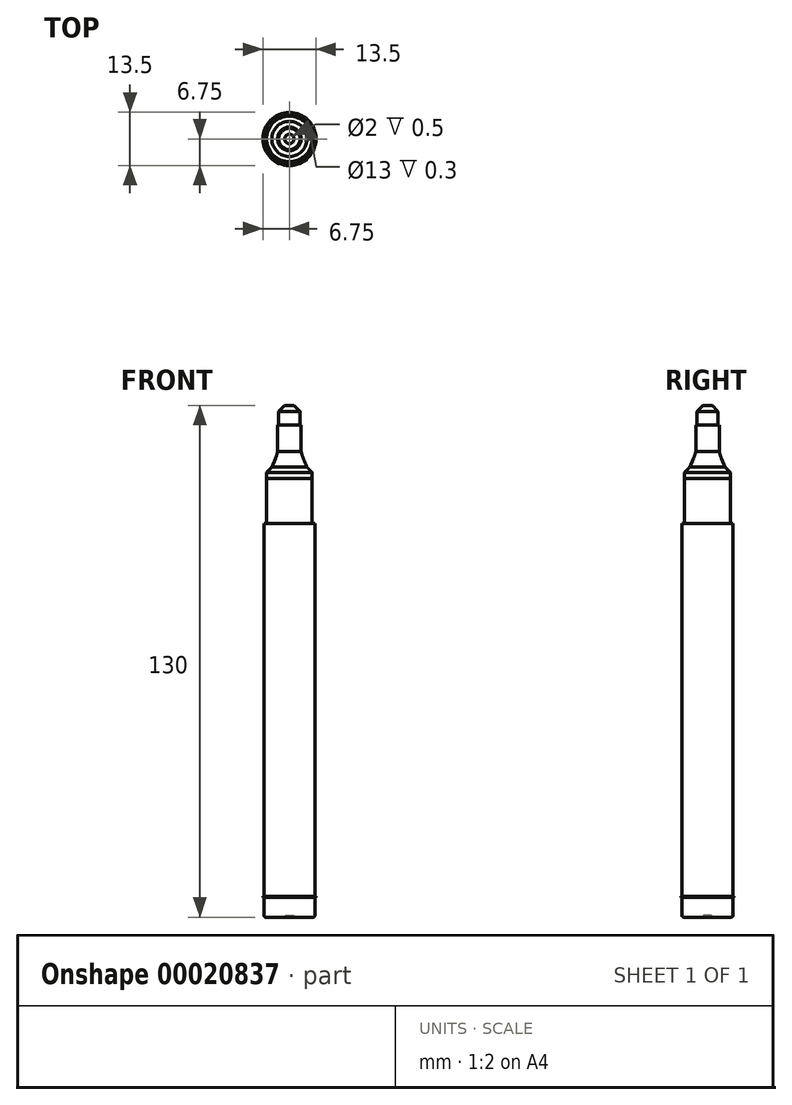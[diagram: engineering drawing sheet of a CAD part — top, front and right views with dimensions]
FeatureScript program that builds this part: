
annotation { "Feature Type Name" : "Feature", "Feature Type Description" : "" }
export const myFeature = defineFeature(function(context is Context, id is Id, definition is map)
    precondition{}
    {
        {
            var Q0;
            Q0=qCreatedBy(makeId("Top.planeOp"),FACE);
            var sketch = newSketch(context, id + "F0", { "sketchPlane" : qUnion([Q0])});
            skCircle(sketch, "E0", {"center": v(0, 0) * mm, "radius": 6.5 * mm});
            skSolve(sketch);
        }
        {
            var Q0;
            Q0 = qSketchRegion(id + "F0", true);
            extrude(context, id + "F1", {"entities" : qUnion([Q0]), "depth" : 5 * mm});
        }
        {
            var Q0;
            Q0=makeQuery(id+"F1.opExtrude","CAP_FACE",FACE,{"disambiguationData":[OSD([sQuery(id+"F0.wireOp",EDGE,"E0")])],"isStart":true});
            var sketch = newSketch(context, id + "F2", { "sketchPlane" : qUnion([Q0])});
            skCircle(sketch, "E1", {"center": v(0, 0) * mm, "radius": 1 * mm});
            skCircle(sketch, "E2", {"center": v(0, 0) * mm, "radius": 0.15 * mm});
            skSolve(sketch);
        }
        {
            var Q0;
            Q0 = qSketchRegion(id + "F2", true);
            extrude(context, id + "F3", {"entities" : qUnion([Q0]), "operationType" : NewBodyOperationType.REMOVE, "oppositeDirection" : true, "depth" : .5 * mm});
        }
        {
            var Q0;
            Q0=makeQuery(id+"F1.opExtrude","CAP_EDGE",EDGE,{"disambiguationData":[OSD([sQuery(id+"F0.wireOp",EDGE,"E0")])],"isStart":true});
            fillet(context, id + "F4", {"entities" : qUnion([Q0]), "radius" : .5 * mm, "tangentPropagation" : true, "allowEdgeOverflow" : false});
        }
        {
            var Q0;
            Q0=makeQuery(id+"F1.opExtrude","CAP_FACE",FACE,{"disambiguationData":[OSD([sQuery(id+"F0.wireOp",EDGE,"E0")])],"isStart":false});
            var sketch = newSketch(context, id + "F5", { "sketchPlane" : qUnion([Q0])});
            skCircle(sketch, "E3", {"center": v(0, 0) * mm, "radius": 6.75 * mm});
            skCircle(sketch, "E4", {"center": v(0, 0) * mm, "radius": 6.5 * mm});
            skSolve(sketch);
        }
        {
            var Q0;
            Q0 = qSketchRegion(id + "F5", true);
            extrude(context, id + "F6", {"entities" : qUnion([Q0]), "depth" : .3 * mm});
        }
        {
            var Q0;
            Q0=makeQuery(id+"F1.opExtrude","CAP_FACE",FACE,{"disambiguationData":[OSD([sQuery(id+"F0.wireOp",EDGE,"E0")])],"isStart":false});
            var sketch = newSketch(context, id + "F7", { "sketchPlane" : qUnion([Q0])});
            skCircle(sketch, "E5", {"center": v(0, 0) * mm, "radius": 6.9 * mm});
            skCircle(sketch, "E6", {"center": v(0, 0) * mm, "radius": 6.75 * mm});
            skSolve(sketch);
        }
        {
            var Q0;
            Q0=sQuery(id+"F7.wireOp",EDGE,"E5");
            var Q1;
            Q1=sQuery(id+"F7.wireOp",EDGE,"E6");
            extrude(context, id + "F8", {"bodyType" : ToolBodyType.SURFACE, "surfaceEntities" : qUnion([Q0, Q1]), "depth" : .5 * mm});
        }
        {
            var Q0;
            Q0=makeQuery(id+"F1.opExtrude","CAP_FACE",FACE,{"disambiguationData":[OSD([sQuery(id+"F0.wireOp",EDGE,"E0")])],"isStart":false});
            var sketch = newSketch(context, id + "F9", { "sketchPlane" : qUnion([Q0])});
            skCircle(sketch, "E7", {"center": v(0, 0) * mm, "radius": 6.5 * mm});
            skSolve(sketch);
        }
        {
            var Q0;
            Q0 = qSketchRegion(id + "F9", true);
            extrude(context, id + "F10", {"entities" : qUnion([Q0]), "depth" : 93 * mm});
        }
        {
            var Q0;
            Q0=makeQuery(id+"F10.opExtrude","CAP_FACE",FACE,{"disambiguationData":[OSD([sQuery(id+"F9.wireOp",EDGE,"E7")])],"isStart":false});
            var sketch = newSketch(context, id + "F11", { "sketchPlane" : qUnion([Q0])});
            skCircle(sketch, "E8", {"center": v(0, 0) * mm, "radius": 6.5 * mm});
            skSolve(sketch);
        }
        {
            var Q0;
            Q0 = qSketchRegion(id + "F11", true);
            extrude(context, id + "F12", {"entities" : qUnion([Q0]), "operationType" : NewBodyOperationType.ADD, "depth" : 2 * mm});
        }
        {
            var Q0;
            Q0=makeQuery(id+"F12.opExtrude","CAP_FACE",FACE,{"disambiguationData":[OSD([sQuery(id+"F11.wireOp",EDGE,"E8")])],"isStart":false});
            var sketch = newSketch(context, id + "F13", { "sketchPlane" : qUnion([Q0])});
            skCircle(sketch, "E9", {"center": v(0, 0) * mm, "radius": 5.8 * mm});
            skSolve(sketch);
        }
        {
            var Q0;
            Q0 = qSketchRegion(id + "F13", true);
            extrude(context, id + "F14", {"entities" : qUnion([Q0]), "depth" : 11.5 * mm});
        }
        {
            var Q0;
            Q0=makeQuery(id+"F14.opExtrude","CAP_FACE",FACE,{"disambiguationData":[OSD([sQuery(id+"F13.wireOp",EDGE,"E9")])],"isStart":false});
            var sketch = newSketch(context, id + "F15", { "sketchPlane" : qUnion([Q0])});
            skCircle(sketch, "E10", {"center": v(0, 0) * mm, "radius": 5.8 * mm});
            skSolve(sketch);
        }
        {
            var Q0;
            Q0 = qSketchRegion(id + "F15", true);
            extrude(context, id + "F16", {"entities" : qUnion([Q0]), "depth" : 6.5 * mm});
        }
        {
            var Q0;
            Q0=makeQuery(id+"F16.opExtrude","CAP_FACE",FACE,{"disambiguationData":[OSD([sQuery(id+"F15.wireOp",EDGE,"E10")])],"isStart":false});
            var sketch = newSketch(context, id + "F17", { "sketchPlane" : qUnion([Q0])});
            skCircle(sketch, "E11", {"center": v(0, 0) * mm, "radius": 3 * mm});
            skSolve(sketch);
        }
        {
            var Q0;
            Q0 = qSketchRegion(id + "F17", true);
            extrude(context, id + "F18", {"entities" : qUnion([Q0]), "operationType" : NewBodyOperationType.ADD, "depth" : 7 * mm});
        }
        {
            var Q0;
            Q0=makeQuery(id+"F16.opExtrude","CAP_EDGE",EDGE,{"disambiguationData":[OSD([sQuery(id+"F15.wireOp",EDGE,"E10")])],"isStart":false});
            chamfer(context, id + "F19", {"entities" : qUnion([Q0]), "width" : 5 * mm, "tangentPropagation" : true});
        }
        {
            var Q0;
            Q0=makeQuery(id+"F19.opChamfer","BLEND_EDGE",EDGE,{"blendedFrom":[makeQuery(id+"F16.opExtrude","CAP_EDGE",EDGE,{"disambiguationData":[OSD([sQuery(id+"F15.wireOp",EDGE,"E10")])],"isStart":false}),makeQuery(id+"F18.opExtrude","SWEPT_FACE",FACE,{"disambiguationData":[OSD([sQuery(id+"F17.wireOp",EDGE,"E11")])]})],"blendedInto":[makeQuery(id+"F18.opExtrude","SWEPT_FACE",FACE,{"disambiguationData":[OSD([sQuery(id+"F17.wireOp",EDGE,"E11")])]})]});
            chamfer(context, id + "F20", {"entities" : qUnion([Q0]), "width" : 5 * mm, "tangentPropagation" : true});
        }
        {
            var Q0;
            {var subQ0=makeQuery(id+"F18.opExtrude","SWEPT_FACE",FACE,{"disambiguationData":[OSD([sQuery(id+"F17.wireOp",EDGE,"E11")])]});Q0=makeQuery(id+"F20.opChamfer","BLEND_EDGE",EDGE,{"blendedFrom":[makeQuery(id+"F19.opChamfer","BLEND_EDGE",EDGE,{"blendedFrom":[makeQuery(id+"F16.opExtrude","CAP_EDGE",EDGE,{"disambiguationData":[OSD([sQuery(id+"F15.wireOp",EDGE,"E10")])],"isStart":false}),subQ0],"blendedInto":[subQ0]}),subQ0],"blendedInto":[subQ0]});}
            chamfer(context, id + "F21", {"entities" : qUnion([Q0]), "width" : 2 * mm, "tangentPropagation" : true});
        }
        {
            var Q0;
            Q0=makeQuery(id+"F18.opExtrude","CAP_FACE",FACE,{"disambiguationData":[OSD([sQuery(id+"F17.wireOp",EDGE,"E11")])],"isStart":false});
            var sketch = newSketch(context, id + "F22", { "sketchPlane" : qUnion([Q0])});
            skCircle(sketch, "E12", {"center": v(0, 0) * mm, "radius": 2.7 * mm});
            skSolve(sketch);
        }
        {
            var Q0;
            Q0 = qSketchRegion(id + "F22", true);
            extrude(context, id + "F23", {"entities" : qUnion([Q0]), "depth" : 5 * mm});
        }
        {
            var Q0;
            {var subQ0=sQuery(id+"F15.wireOp",EDGE,"E10");var subQ1=sQuery(id+"F17.wireOp",EDGE,"E11");var subQ2=makeQuery(id+"F18.opExtrude","SWEPT_FACE",FACE,{"disambiguationData":[OSD([subQ1])]});Q0=makeQuery(id+"F21.opChamfer","BLEND_EDGE",EDGE,{"blendedFrom":[makeQuery(id+"F20.opChamfer","BLEND_EDGE",EDGE,{"blendedFrom":[makeQuery(id+"F19.opChamfer","BLEND_EDGE",EDGE,{"blendedFrom":[makeQuery(id+"F16.opExtrude","CAP_EDGE",EDGE,{"disambiguationData":[OSD([subQ0])],"isStart":false}),subQ2],"blendedInto":[subQ2]}),subQ2],"blendedInto":[subQ2]}),makeQuery(id+"F20.opChamfer","BLEND_FACE",FACE,{"disambiguationData":[OSD([subQ0,subQ1])]})],"blendedInto":[makeQuery(id+"F20.opChamfer","BLEND_FACE",FACE,{"disambiguationData":[OSD([subQ0,subQ1])]})]});}
            fillet(context, id + "F24", {"entities" : qUnion([Q0]), "radius" : 10 * mm, "tangentPropagation" : true, "allowEdgeOverflow" : false});
        }
        {
            var Q0;
            Q0=makeQuery(id+"F23.opExtrude","CAP_EDGE",EDGE,{"disambiguationData":[OSD([sQuery(id+"F22.wireOp",EDGE,"E12")])],"isStart":false});
            chamfer(context, id + "F25", {"entities" : qUnion([Q0]), "width" : 1.5 * mm, "tangentPropagation" : true});
        }
    });
